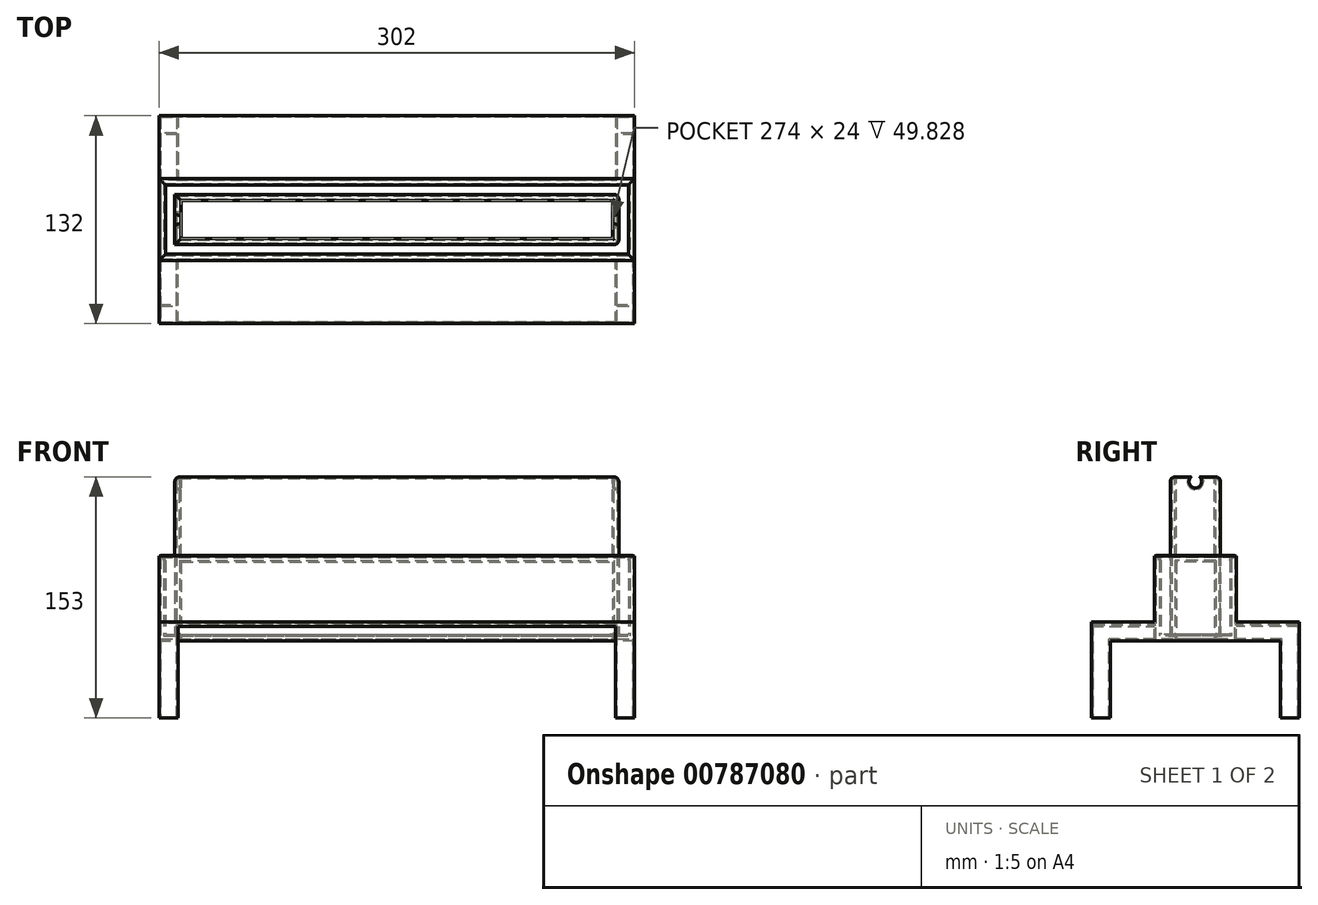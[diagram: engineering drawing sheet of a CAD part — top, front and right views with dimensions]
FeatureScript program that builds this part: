
annotation { "Feature Type Name" : "Feature", "Feature Type Description" : "" }
export const myFeature = defineFeature(function(context is Context, id is Id, definition is map)
    precondition{}
    {
        {
            var Q0;
            Q0=qCreatedBy(makeId("Top.planeOp"),FACE);
            var sketch = newSketch(context, id + "F0", { "sketchPlane" : qUnion([Q0])});
            skLineSegment(sketch, "E0.bottom", {"start": v(-150, 25) * mm, "end": v(150, 25) * mm});
            skLineSegment(sketch, "E0.top", {"start": v(-150, -25) * mm, "end": v(150, -25) * mm});
            skLineSegment(sketch, "E0.left", {"start": v(-150, 25) * mm, "end": v(-150, -25) * mm});
            skLineSegment(sketch, "E0.right", {"start": v(150, 25) * mm, "end": v(150, -25) * mm});
            skSolve(sketch);
        }
        {
            var Q0;
            Q0 = qSketchRegion(id + "F0", true);
            extrude(context, id + "F1", {"entities" : qUnion([Q0]), "depth" : 2 * mm, "offsetDistance" : 25 * mm});
        }
        {
            var Q0;
            Q0=makeQuery(id+"F1.opExtrude","CAP_FACE",FACE,{"disambiguationData":[OSD([sQuery(id+"F0.wireOp",EDGE,"E0.bottom"),sQuery(id+"F0.wireOp",EDGE,"E0.top"),sQuery(id+"F0.wireOp",EDGE,"E0.left"),sQuery(id+"F0.wireOp",EDGE,"E0.right")])],"isStart":false});
            var sketch = newSketch(context, id + "F2", { "sketchPlane" : qUnion([Q0])});
            skLineSegment(sketch, "E1.bottom", {"start": v(-150, 25) * mm, "end": v(150, 25) * mm});
            skLineSegment(sketch, "E1.top", {"start": v(-150, -25) * mm, "end": v(150, -25) * mm});
            skLineSegment(sketch, "E1.left", {"start": v(-150, 25) * mm, "end": v(-150, -25) * mm});
            skLineSegment(sketch, "E1.right", {"start": v(150, 25) * mm, "end": v(150, -25) * mm});
            skLineSegment(sketch, "E2.bottom", {"start": v(-148, 23) * mm, "end": v(148, 23) * mm});
            skLineSegment(sketch, "E2.top", {"start": v(-148, -23) * mm, "end": v(148, -23) * mm});
            skLineSegment(sketch, "E2.left", {"start": v(-148, 23) * mm, "end": v(-148, -23) * mm});
            skLineSegment(sketch, "E2.right", {"start": v(148, 23) * mm, "end": v(148, -23) * mm});
            skSolve(sketch);
        }
        {
            var Q0;
            Q0 = qSketchRegion(id + "F2", true);
            extrude(context, id + "F3", {"entities" : qUnion([Q0]), "operationType" : NewBodyOperationType.ADD, "depth" : 50 * mm, "offsetDistance" : 25 * mm});
        }
        {
            var Q0;
            Q0=makeQuery(id+"F1.opExtrude","CAP_FACE",FACE,{"disambiguationData":[OSD([sQuery(id+"F0.wireOp",EDGE,"E0.bottom"),sQuery(id+"F0.wireOp",EDGE,"E0.top"),sQuery(id+"F0.wireOp",EDGE,"E0.left"),sQuery(id+"F0.wireOp",EDGE,"E0.right")])],"isStart":false});
            var sketch = newSketch(context, id + "F4", { "sketchPlane" : qUnion([Q0])});
            skLineSegment(sketch, "E3.bottom", {"start": v(-140, 15) * mm, "end": v(140, 15) * mm});
            skLineSegment(sketch, "E3.top", {"start": v(-140, -15) * mm, "end": v(140, -15) * mm});
            skLineSegment(sketch, "E3.left", {"start": v(-140, 15) * mm, "end": v(-140, -15) * mm});
            skLineSegment(sketch, "E3.right", {"start": v(140, 15) * mm, "end": v(140, -15) * mm});
            skSolve(sketch);
        }
        {
            var Q0;
            Q0 = qSketchRegion(id + "F4", true);
            extrude(context, id + "F5", {"entities" : qUnion([Q0]), "operationType" : NewBodyOperationType.ADD, "depth" : 100 * mm, "offsetDistance" : 25 * mm});
        }
        {
            var Q0;
            Q0=makeQuery(id+"F5.opExtrude","CAP_FACE",FACE,{"disambiguationData":[OSD([sQuery(id+"F4.wireOp",EDGE,"E3.bottom"),sQuery(id+"F4.wireOp",EDGE,"E3.top"),sQuery(id+"F4.wireOp",EDGE,"E3.left"),sQuery(id+"F4.wireOp",EDGE,"E3.right")])],"isStart":false});
            var sketch = newSketch(context, id + "F6", { "sketchPlane" : qUnion([Q0])});
            skLineSegment(sketch, "E4.bottom", {"start": v(-138, 13) * mm, "end": v(138, 13) * mm});
            skLineSegment(sketch, "E4.top", {"start": v(-138, -13) * mm, "end": v(138, -13) * mm});
            skLineSegment(sketch, "E4.left", {"start": v(-138, 13) * mm, "end": v(-138, -13) * mm});
            skLineSegment(sketch, "E4.right", {"start": v(138, 13) * mm, "end": v(138, -13) * mm});
            skSolve(sketch);
        }
        {
            var Q0;
            Q0 = qSketchRegion(id + "F6", true);
            extrude(context, id + "F7", {"entities" : qUnion([Q0]), "operationType" : NewBodyOperationType.REMOVE, "oppositeDirection" : true, "depth" : 50 * mm, "offsetDistance" : 25 * mm});
        }
        {
            var Q0;
            Q0=makeQuery(id+"F1.opExtrude","CAP_FACE",FACE,{"disambiguationData":[OSD([sQuery(id+"F0.wireOp",EDGE,"E0.bottom"),sQuery(id+"F0.wireOp",EDGE,"E0.top"),sQuery(id+"F0.wireOp",EDGE,"E0.left"),sQuery(id+"F0.wireOp",EDGE,"E0.right")])],"isStart":true});
            shell(context, id + "F8", {"entities" : qUnion([Q0]), "thickness" : 2 * mm});
        }
        {
            var Q0;
            Q0=makeQuery(id+"F5.opExtrude","CAP_EDGE",EDGE,{"disambiguationData":[OSD([sQuery(id+"F4.wireOp",EDGE,"E3.top")])],"isStart":false});
            var Q1;
            Q1=makeQuery(id+"F5.opExtrude","CAP_EDGE",EDGE,{"disambiguationData":[OSD([sQuery(id+"F4.wireOp",EDGE,"E3.bottom")])],"isStart":false});
            var Q2;
            Q2=makeQuery(id+"F3.opExtrude","CAP_EDGE",EDGE,{"disambiguationData":[OSD([sQuery(id+"F2.wireOp",EDGE,"E2.top")])],"isStart":false});
            var Q3;
            Q3=makeQuery(id+"F3.opExtrude","CAP_EDGE",EDGE,{"disambiguationData":[OSD([sQuery(id+"F2.wireOp",EDGE,"E2.right")])],"isStart":false});
            var Q4;
            Q4=makeQuery(id+"F3.opExtrude","CAP_EDGE",EDGE,{"disambiguationData":[OSD([sQuery(id+"F2.wireOp",EDGE,"E2.bottom")])],"isStart":false});
            var Q5;
            Q5=makeQuery(id+"F3.opExtrude","CAP_EDGE",EDGE,{"disambiguationData":[OSD([sQuery(id+"F2.wireOp",EDGE,"E2.left")])],"isStart":false});
            var Q6;
            Q6=makeQuery(id+"F5.opExtrude","SWEPT_FACE",FACE,{"disambiguationData":[OSD([sQuery(id+"F4.wireOp",EDGE,"E3.right")])]});
            var Q7;
            Q7=makeQuery(id+"F5.opExtrude","CAP_EDGE",EDGE,{"disambiguationData":[OSD([sQuery(id+"F4.wireOp",EDGE,"E3.left")])],"isStart":false});
            fillet(context, id + "F9", {"entities" : qUnion([Q0, Q1, Q2, Q3, Q4, Q5, Q6, Q7]), "radius" : 2 * mm, "tangentPropagation" : true, "allowEdgeOverflow" : false});
        }
        {
            var Q0;
            Q0=makeQuery(id+"F5.opExtrude","SWEPT_FACE",FACE,{"disambiguationData":[OSD([sQuery(id+"F4.wireOp",EDGE,"E3.right")])]});
            var sketch = newSketch(context, id + "F10", { "sketchPlane" : qUnion([Q0])});
            skCircle(sketch, "E5", {"center": v(0, 100) * mm, "radius": 5 * mm});
            skSolve(sketch);
        }
        {
            var Q0;
            Q0 = qSketchRegion(id + "F10", true);
            extrude(context, id + "F11", {"entities" : qUnion([Q0]), "operationType" : NewBodyOperationType.REMOVE, "oppositeDirection" : true, "depth" : 300 * mm, "offsetDistance" : 25 * mm});
        }
        {
            var Q0;
            Q0=makeQuery(id+"F3.boolean.opBoolean","MERGE",FACE,{"derivedFrom":[makeQuery(id+"F1.opExtrude","SWEPT_FACE",FACE,{"disambiguationData":[OSD([sQuery(id+"F0.wireOp",EDGE,"E0.top")])]}),makeQuery(id+"F3.opExtrude","SWEPT_FACE",FACE,{"disambiguationData":[OSD([sQuery(id+"F2.wireOp",EDGE,"E1.top")])]})]});
            var sketch = newSketch(context, id + "F12", { "sketchPlane" : qUnion([Q0])});
            skLineSegment(sketch, "E6.bottom", {"start": v(-150, 0) * mm, "end": v(-140, 0) * mm});
            skLineSegment(sketch, "E6.top", {"start": v(-150, 10) * mm, "end": v(-140, 10) * mm});
            skLineSegment(sketch, "E6.left", {"start": v(-150, 0) * mm, "end": v(-150, 10) * mm});
            skLineSegment(sketch, "E6.right", {"start": v(-140, 0) * mm, "end": v(-140, 10) * mm});
            skLineSegment(sketch, "E7.bottom", {"start": v(150, 0) * mm, "end": v(140, 0) * mm});
            skLineSegment(sketch, "E7.top", {"start": v(150, 10) * mm, "end": v(140, 10) * mm});
            skLineSegment(sketch, "E7.left", {"start": v(150, 0) * mm, "end": v(150, 10) * mm});
            skLineSegment(sketch, "E7.right", {"start": v(140, 0) * mm, "end": v(140, 10) * mm});
            skSolve(sketch);
        }
        {
            var Q0;
            Q0=makeQuery(id+"F3.boolean.opBoolean","MERGE",FACE,{"derivedFrom":[makeQuery(id+"F1.opExtrude","SWEPT_FACE",FACE,{"disambiguationData":[OSD([sQuery(id+"F0.wireOp",EDGE,"E0.bottom")])]}),makeQuery(id+"F3.opExtrude","SWEPT_FACE",FACE,{"disambiguationData":[OSD([sQuery(id+"F2.wireOp",EDGE,"E1.bottom")])]})]});
            var sketch = newSketch(context, id + "F13", { "sketchPlane" : qUnion([Q0])});
            skLineSegment(sketch, "E8.bottom", {"start": v(-150, 0) * mm, "end": v(-140, 0) * mm});
            skLineSegment(sketch, "E8.top", {"start": v(-150, 10) * mm, "end": v(-140, 10) * mm});
            skLineSegment(sketch, "E8.left", {"start": v(-150, 0) * mm, "end": v(-150, 10) * mm});
            skLineSegment(sketch, "E8.right", {"start": v(-140, 0) * mm, "end": v(-140, 10) * mm});
            skLineSegment(sketch, "E9.bottom", {"start": v(150, 0) * mm, "end": v(140, 0) * mm});
            skLineSegment(sketch, "E9.top", {"start": v(150, 10) * mm, "end": v(140, 10) * mm});
            skLineSegment(sketch, "E9.left", {"start": v(150, 0) * mm, "end": v(150, 10) * mm});
            skLineSegment(sketch, "E9.right", {"start": v(140, 0) * mm, "end": v(140, 10) * mm});
            skSolve(sketch);
        }
        {
            var Q0;
            Q0 = qSketchRegion(id + "F12", true);
            extrude(context, id + "F14", {"entities" : qUnion([Q0]), "operationType" : NewBodyOperationType.ADD, "depth" : 40 * mm, "offsetDistance" : 25 * mm});
        }
        {
            var Q0;
            Q0 = qSketchRegion(id + "F13", true);
            extrude(context, id + "F15", {"entities" : qUnion([Q0]), "operationType" : NewBodyOperationType.ADD, "depth" : 40 * mm, "offsetDistance" : 25 * mm});
        }
        {
            var Q0;
            Q0=makeQuery(id+"F15.boolean.opBoolean","MERGE",FACE,{"derivedFrom":[makeQuery(id+"F14.boolean.opBoolean","MERGE",FACE,{"derivedFrom":[makeQuery(id+"F1.opExtrude","CAP_FACE",FACE,{"disambiguationData":[OSD([sQuery(id+"F0.wireOp",EDGE,"E0.bottom"),sQuery(id+"F0.wireOp",EDGE,"E0.top"),sQuery(id+"F0.wireOp",EDGE,"E0.left"),sQuery(id+"F0.wireOp",EDGE,"E0.right")])],"isStart":true}),makeQuery(id+"F14.opExtrude","SWEPT_FACE",FACE,{"disambiguationData":[OSD([sQuery(id+"F12.wireOp",EDGE,"E6.bottom")])]}),makeQuery(id+"F14.opExtrude","SWEPT_FACE",FACE,{"disambiguationData":[OSD([sQuery(id+"F12.wireOp",EDGE,"E7.bottom")])]})]}),makeQuery(id+"F15.opExtrude","SWEPT_FACE",FACE,{"disambiguationData":[OSD([sQuery(id+"F13.wireOp",EDGE,"E8.bottom")])]}),makeQuery(id+"F15.opExtrude","SWEPT_FACE",FACE,{"disambiguationData":[OSD([sQuery(id+"F13.wireOp",EDGE,"E9.bottom")])]})]});
            var sketch = newSketch(context, id + "F16", { "sketchPlane" : qUnion([Q0])});
            skLineSegment(sketch, "E10.bottom", {"start": v(140, 65) * mm, "end": v(150, 65) * mm});
            skLineSegment(sketch, "E10.top", {"start": v(140, 55) * mm, "end": v(150, 55) * mm});
            skLineSegment(sketch, "E10.left", {"start": v(140, 65) * mm, "end": v(140, 55) * mm});
            skLineSegment(sketch, "E10.right", {"start": v(150, 65) * mm, "end": v(150, 55) * mm});
            skLineSegment(sketch, "E11.bottom", {"start": v(150, -65) * mm, "end": v(140, -65) * mm});
            skLineSegment(sketch, "E11.top", {"start": v(150, -55) * mm, "end": v(140, -55) * mm});
            skLineSegment(sketch, "E11.left", {"start": v(150, -65) * mm, "end": v(150, -55) * mm});
            skLineSegment(sketch, "E11.right", {"start": v(140, -65) * mm, "end": v(140, -55) * mm});
            skLineSegment(sketch, "E12.bottom", {"start": v(-140, -65) * mm, "end": v(-150, -65) * mm});
            skLineSegment(sketch, "E12.top", {"start": v(-140, -55) * mm, "end": v(-150, -55) * mm});
            skLineSegment(sketch, "E12.left", {"start": v(-140, -65) * mm, "end": v(-140, -55) * mm});
            skLineSegment(sketch, "E12.right", {"start": v(-150, -65) * mm, "end": v(-150, -55) * mm});
            skLineSegment(sketch, "E13.bottom", {"start": v(-150, 65) * mm, "end": v(-140, 65) * mm});
            skLineSegment(sketch, "E13.top", {"start": v(-150, 55) * mm, "end": v(-140, 55) * mm});
            skLineSegment(sketch, "E13.left", {"start": v(-150, 65) * mm, "end": v(-150, 55) * mm});
            skLineSegment(sketch, "E13.right", {"start": v(-140, 65) * mm, "end": v(-140, 55) * mm});
            skSolve(sketch);
        }
        {
            var Q0;
            Q0 = qSketchRegion(id + "F16", true);
            extrude(context, id + "F17", {"entities" : qUnion([Q0]), "operationType" : NewBodyOperationType.ADD, "depth" : 50 * mm, "offsetDistance" : 25 * mm});
        }
        {
            var Q0;
            Q0=makeQuery(id+"F17.boolean.opBoolean","MERGE",FACE,{"derivedFrom":[makeQuery(id+"F14.opExtrude","SWEPT_FACE",FACE,{"disambiguationData":[OSD([sQuery(id+"F12.wireOp",EDGE,"E6.right")])]}),makeQuery(id+"F17.opExtrude","SWEPT_FACE",FACE,{"disambiguationData":[OSD([sQuery(id+"F16.wireOp",EDGE,"E13.right")])]})]});
            var sketch = newSketch(context, id + "F18", { "sketchPlane" : qUnion([Q0])});
            skLineSegment(sketch, "E14.bottom", {"start": v(-65, 10) * mm, "end": v(-25, 10) * mm});
            skLineSegment(sketch, "E14.top", {"start": v(-65, 9) * mm, "end": v(-25, 9) * mm});
            skLineSegment(sketch, "E14.left", {"start": v(-65, 10) * mm, "end": v(-65, 9) * mm});
            skLineSegment(sketch, "E14.right", {"start": v(-25, 10) * mm, "end": v(-25, 9) * mm});
            skSolve(sketch);
        }
        {
            var Q0;
            Q0=makeQuery(id+"F17.boolean.opBoolean","MERGE",FACE,{"derivedFrom":[makeQuery(id+"F15.opExtrude","SWEPT_FACE",FACE,{"disambiguationData":[OSD([sQuery(id+"F13.wireOp",EDGE,"E9.right")])]}),makeQuery(id+"F17.opExtrude","SWEPT_FACE",FACE,{"disambiguationData":[OSD([sQuery(id+"F16.wireOp",EDGE,"E12.left")])]})]});
            var sketch = newSketch(context, id + "F19", { "sketchPlane" : qUnion([Q0])});
            skLineSegment(sketch, "E15.bottom", {"start": v(65, 10) * mm, "end": v(25, 10) * mm});
            skLineSegment(sketch, "E15.top", {"start": v(65, 9) * mm, "end": v(25, 9) * mm});
            skLineSegment(sketch, "E15.left", {"start": v(65, 10) * mm, "end": v(65, 9) * mm});
            skLineSegment(sketch, "E15.right", {"start": v(25, 10) * mm, "end": v(25, 9) * mm});
            skSolve(sketch);
        }
        {
            var Q0;
            Q0 = qSketchRegion(id + "F19", true);
            var Q1;
            Q1 = qSketchRegion(id + "F18", true);
            extrude(context, id + "F20", {"entities" : qUnion([Q0, Q1]), "operationType" : NewBodyOperationType.ADD, "depth" : 280 * mm, "offsetDistance" : 25 * mm});
        }
        {
            var Q0;
            Q0=makeQuery(id+"F17.opExtrude","CAP_FACE",FACE,{"disambiguationData":[OSD([sQuery(id+"F16.wireOp",EDGE,"E12.bottom"),sQuery(id+"F16.wireOp",EDGE,"E12.top"),sQuery(id+"F16.wireOp",EDGE,"E12.left"),sQuery(id+"F16.wireOp",EDGE,"E12.right")])],"isStart":false});
            var Q1;
            Q1=makeQuery(id+"F17.opExtrude","CAP_FACE",FACE,{"disambiguationData":[OSD([sQuery(id+"F16.wireOp",EDGE,"E13.bottom"),sQuery(id+"F16.wireOp",EDGE,"E13.top"),sQuery(id+"F16.wireOp",EDGE,"E13.left"),sQuery(id+"F16.wireOp",EDGE,"E13.right")])],"isStart":false});
            var Q2;
            Q2=makeQuery(id+"F17.opExtrude","CAP_FACE",FACE,{"disambiguationData":[OSD([sQuery(id+"F16.wireOp",EDGE,"E10.bottom"),sQuery(id+"F16.wireOp",EDGE,"E10.top"),sQuery(id+"F16.wireOp",EDGE,"E10.left"),sQuery(id+"F16.wireOp",EDGE,"E10.right")])],"isStart":false});
            var Q3;
            Q3=makeQuery(id+"F17.opExtrude","CAP_FACE",FACE,{"disambiguationData":[OSD([sQuery(id+"F16.wireOp",EDGE,"E11.bottom"),sQuery(id+"F16.wireOp",EDGE,"E11.top"),sQuery(id+"F16.wireOp",EDGE,"E11.left"),sQuery(id+"F16.wireOp",EDGE,"E11.right")])],"isStart":false});
            shell(context, id + "F21", {"entities" : qUnion([Q0, Q1, Q2, Q3]), "thickness" : 1 * mm, "oppositeDirection" : true});
        }
    });
